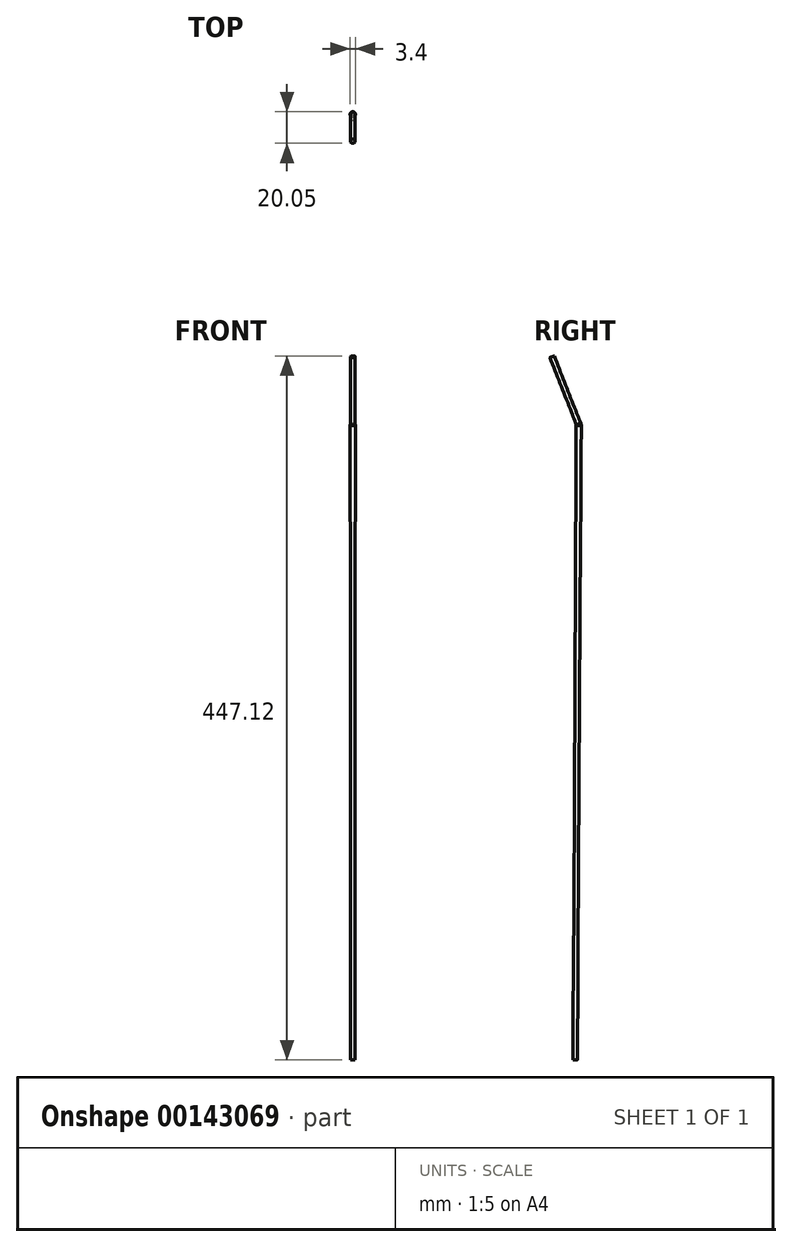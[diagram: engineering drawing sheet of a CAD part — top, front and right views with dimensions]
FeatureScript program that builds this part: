
annotation { "Feature Type Name" : "Feature", "Feature Type Description" : "" }
export const myFeature = defineFeature(function(context is Context, id is Id, definition is map)
    precondition{}
    {
        {
            var Q0;
            Q0=qCreatedBy(makeId("Top.planeOp"),FACE);
            cPlane(context, id + "F0", {"entities" : qUnion([Q0]), "cplaneType" : CPlaneType.OFFSET, "offset" : 403 * mm, "width" : 150 * mm, "height" : 150 * mm});
        }
        {
            var Q0;
            Q0=qCreatedBy(id+"F0.planeOp",FACE);
            var sketch = newSketch(context, id + "F1", { "sketchPlane" : qUnion([Q0])});
            skLineSegment(sketch, "E0", {"start": v(-34.1, 0) * mm, "end": v(37.39, 0) * mm});
            skSolve(sketch);
        }
        {
            var Q0;
            Q0=sQuery(id+"F1.wireOp",EDGE,"E0");
            cPlane(context, id + "F2", {"entities" : qUnion([Q0]), "cplaneType" : CPlaneType.LINE_ANGLE, "offset" : 25 * mm, "angle" : 110 * degree, "width" : 150 * mm, "height" : 150 * mm});
        }
        {
            var Q0;
            Q0=qCreatedBy(id+"F0.planeOp",FACE);
            var sketch = newSketch(context, id + "F3", { "sketchPlane" : qUnion([Q0])});
            skCircle(sketch, "E1", {"center": v(-6.3, 1.03) * mm, "radius": 1.5 * mm});
            skCircle(sketch, "E2", {"center": v(-22.45, 2.24) * mm, "radius": 1.7 * mm});
            skCircle(sketch, "E3", {"center": v(9.7, 1.03) * mm, "radius": 1.5 * mm});
            skCircle(sketch, "E4", {"center": v(25.7, 1.03) * mm, "radius": 1.5 * mm});
            skSolve(sketch);
        }
        {
            var Q0;
            Q0=qCreatedBy(id+"F2.planeOp",FACE);
            var sketch = newSketch(context, id + "F4", { "sketchPlane" : qUnion([Q0])});
            skCircle(sketch, "E5", {"center": v(-6.37, 139.98) * mm, "radius": 1.5 * mm});
            skCircle(sketch, "E6", {"center": v(-22.37, 140.13) * mm, "radius": 1.5 * mm});
            skCircle(sketch, "E7", {"center": v(9.6, 139) * mm, "radius": 1.5 * mm});
            skCircle(sketch, "E8", {"center": v(25.6, 139) * mm, "radius": 1.5 * mm});
            skSolve(sketch);
        }
        {
            var Q0;
            Q0=qCreatedBy(id+"F2.planeOp",FACE);
            cPlane(context, id + "F5", {"entities" : qUnion([Q0]), "cplaneType" : CPlaneType.OFFSET, "offset" : 46 * mm, "width" : 150 * mm, "height" : 150 * mm});
        }
        {
            var Q0;
            Q0=qCreatedBy(id+"F5.planeOp",FACE);
            var sketch = newSketch(context, id + "F6", { "sketchPlane" : qUnion([Q0])});
            skCircle(sketch, "E9", {"center": v(-22.4, 138.94) * mm, "radius": 1.5 * mm});
            skSolve(sketch);
        }
        {
            var Q0;
            Q0=qCreatedBy(makeId("Top.planeOp"),FACE);
            var sketch = newSketch(context, id + "F7", { "sketchPlane" : qUnion([Q0])});
            skCircle(sketch, "E10", {"center": v(-22.34, 0) * mm, "radius": 1.5 * mm});
            skSolve(sketch);
        }
        {
            var Q0;
            Q0=makeQuery(id+"F7.imprint","IMPRINT",FACE,{"disambiguationData":[TD([[makeQuery(id+"F7.imprint","IMPRINT",EDGE,{"derivedFrom":sQuery(id+"F7.wireOp",EDGE,"E10")}),1.0]])]});
            var Q1;
            Q1=makeQuery(id+"F3.imprint","IMPRINT",FACE,{"disambiguationData":[TD([[makeQuery(id+"F3.imprint","IMPRINT",EDGE,{"derivedFrom":sQuery(id+"F3.wireOp",EDGE,"E2")}),1.0]])]});
            loft(context, id + "F8", {"sheetProfilesArray" : [{ "sheetProfileEntities" : qUnion([Q0]) }, { "sheetProfileEntities" : qUnion([Q1]) }]});
        }
        {
            var Q1;
            Q1=makeQuery(id+"F3.imprint","IMPRINT",FACE,{"disambiguationData":[TD([[makeQuery(id+"F3.imprint","IMPRINT",EDGE,{"derivedFrom":sQuery(id+"F3.wireOp",EDGE,"E2")}),1.0]])]});
            var Q2;
            Q2=makeQuery(id+"F4.imprint","IMPRINT",FACE,{"disambiguationData":[TD([[makeQuery(id+"F4.imprint","IMPRINT",EDGE,{"derivedFrom":sQuery(id+"F4.wireOp",EDGE,"E6")}),1.0]])]});
            loft(context, id + "F9", {"operationType" : NewBodyOperationType.ADD, "sheetProfilesArray" : [{ "sheetProfileEntities" : qUnion([Q1]) }, { "sheetProfileEntities" : qUnion([Q2]) }]});
        }
        {
            var Q1;
            Q1=makeQuery(id+"F9.opLoft","CAP_FACE",FACE,{"disambiguationData":[OSD([makeQuery(id+"F4.imprint","IMPRINT",FACE,{"disambiguationData":[TD([[makeQuery(id+"F4.imprint","IMPRINT",EDGE,{"derivedFrom":sQuery(id+"F4.wireOp",EDGE,"E6")}),1.0]])]})])],"isStart":true});
            var Q2;
            Q2=makeQuery(id+"F6.imprint","IMPRINT",FACE,{"disambiguationData":[TD([[makeQuery(id+"F6.imprint","IMPRINT",EDGE,{"derivedFrom":sQuery(id+"F6.wireOp",EDGE,"E9")}),1.0]])]});
            loft(context, id + "F10", {"operationType" : NewBodyOperationType.ADD, "sheetProfilesArray" : [{ "sheetProfileEntities" : qUnion([Q1]) }, { "sheetProfileEntities" : qUnion([Q2]) }]});
        }
    });
